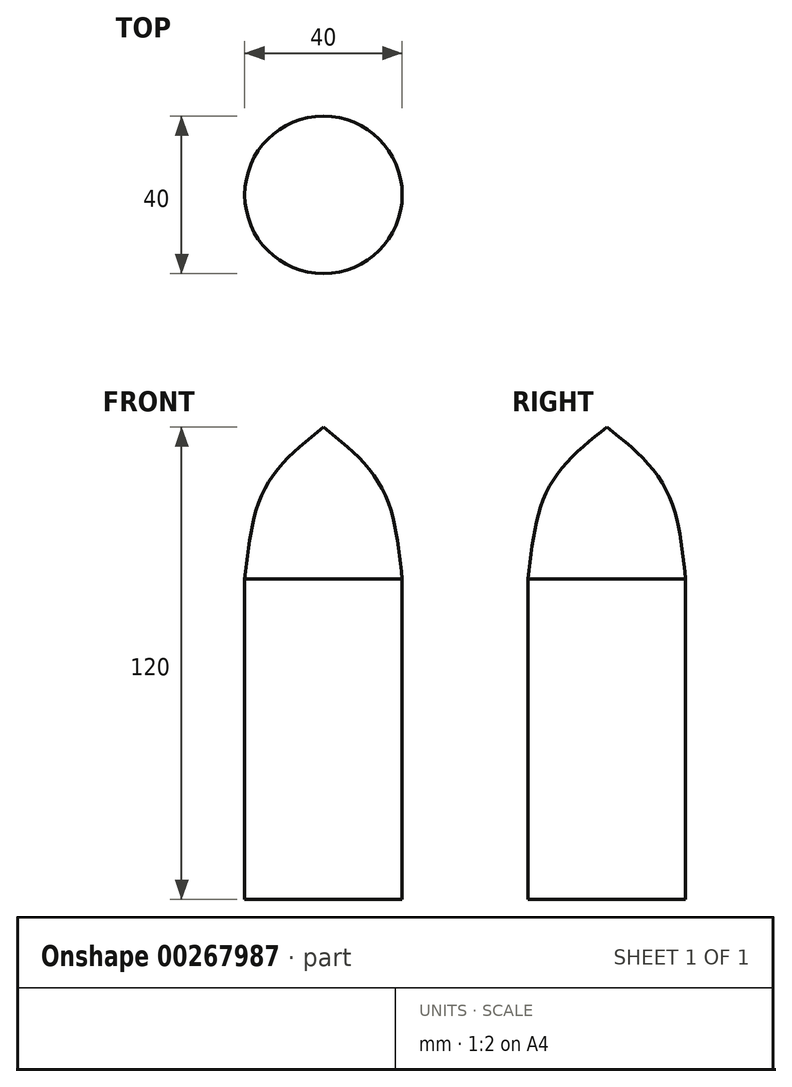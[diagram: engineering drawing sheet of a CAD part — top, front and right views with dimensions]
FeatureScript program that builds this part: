
annotation { "Feature Type Name" : "Feature", "Feature Type Description" : "" }
export const myFeature = defineFeature(function(context is Context, id is Id, definition is map)
    precondition{}
    {
        {
            var Q0;
            Q0=qCreatedBy(makeId("Right.planeOp"),FACE);
            var sketch = newSketch(context, id + "F0", { "sketchPlane" : qUnion([Q0])});
            skLineSegment(sketch, "E0", {"start": v(0, 0) * mm, "end": v(0, 81.38) * mm});
            skLineSegment(sketch, "E1", {"start": v(20, 120) * mm, "end": v(20, 0) * mm, "construction": true});
            skLineSegment(sketch, "E2", {"start": v(20, 0) * mm, "end": v(0, 0) * mm});
            skPoint(sketch, "E3", {"position": v(0, 81.38) * mm});
            skFitSpline(sketch, "E4", {"points": [v(0, 81.38) * mm, v(5.28, 104.71) * mm, v(20, 120) * mm], "startDerivative": vector(5.08, 48.85) * mm, "endDerivative": vector(35.22, 28.17) * mm});
            skLineSegment(sketch, "E5", {"start": v(20, 120) * mm, "end": v(20, 0) * mm});
            skSolve(sketch);
        }
        {
            var Q0;
            Q0=makeQuery(id+"F0.imprint","IMPRINT",FACE,{"disambiguationData":[TD([[makeQuery(id+"F0.imprint","IMPRINT",EDGE,{"derivedFrom":sQuery(id+"F0.wireOp",EDGE,"E0")}),-1.0]])]});
            var Q1;
            Q1=sQuery(id+"F0.wireOp",EDGE,"E5");
            revolve(context, id + "F1", {"entities" : qUnion([Q0]), "axis" : qUnion([Q1]), "revolveType" : RevolveType.FULL});
        }
    });
